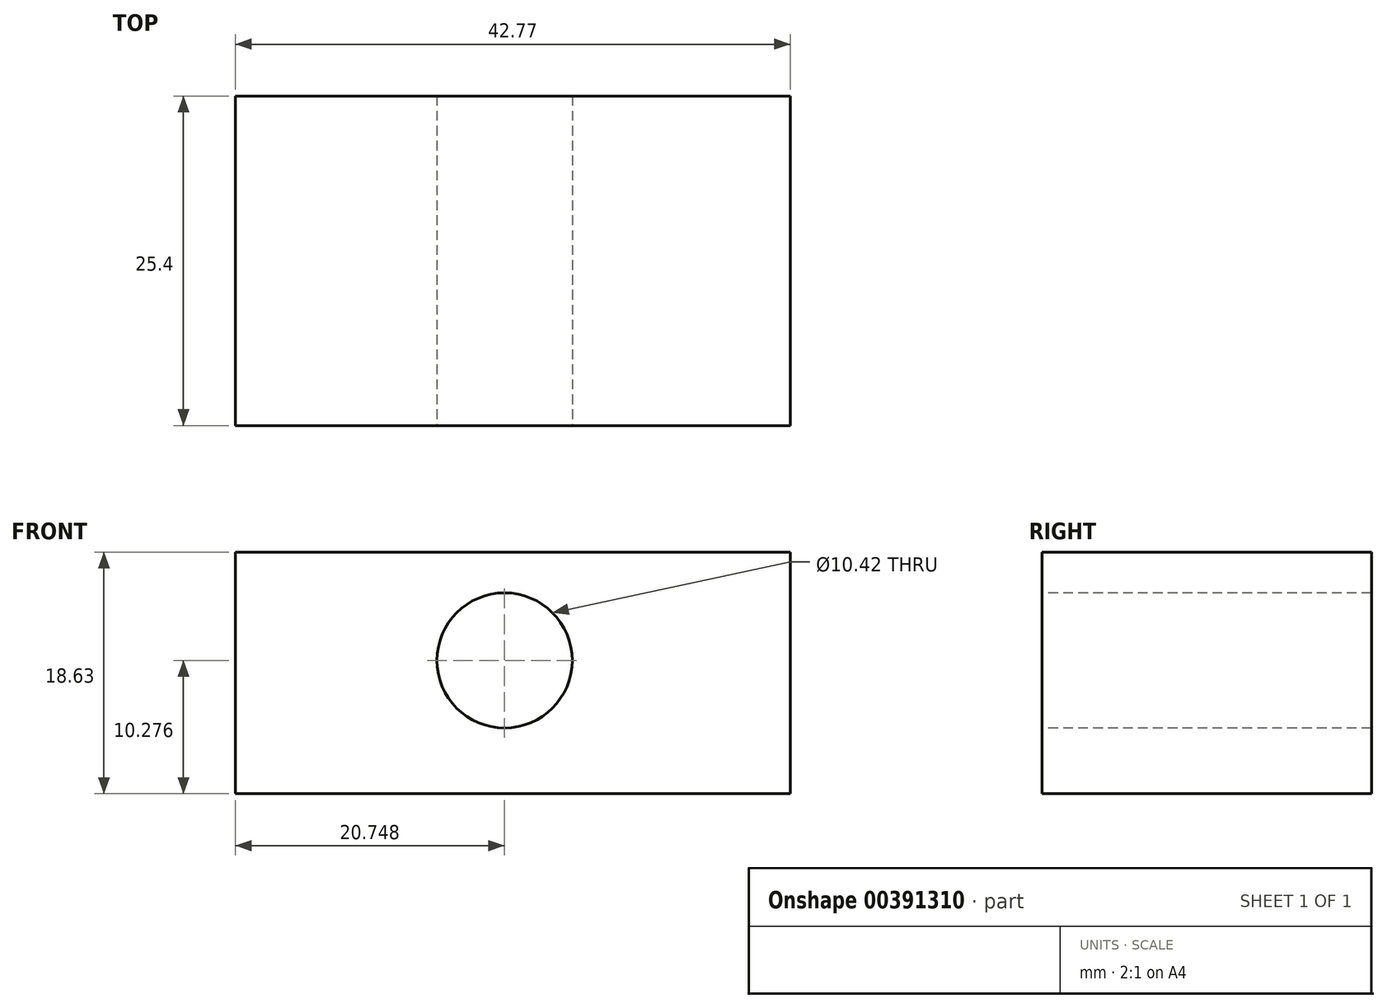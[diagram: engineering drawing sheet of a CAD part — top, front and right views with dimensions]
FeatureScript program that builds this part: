
annotation { "Feature Type Name" : "Feature", "Feature Type Description" : "" }
export const myFeature = defineFeature(function(context is Context, id is Id, definition is map)
    precondition{}
    {
        {
            var Q0;
            Q0=qCreatedBy(makeId("Front.planeOp"),FACE);
            var sketch = newSketch(context, id + "F0", { "sketchPlane" : qUnion([Q0])});
            skLineSegment(sketch, "E0.bottom", {"start": v(0, 0) * mm, "end": v(-42.77, 0) * mm});
            skLineSegment(sketch, "E0.top", {"start": v(0, 18.63) * mm, "end": v(-42.77, 18.63) * mm});
            skLineSegment(sketch, "E0.left", {"start": v(0, 0) * mm, "end": v(0, 18.63) * mm});
            skLineSegment(sketch, "E0.right", {"start": v(-42.77, 0) * mm, "end": v(-42.77, 18.63) * mm});
            skCircle(sketch, "E1", {"center": v(-22.02, 10.28) * mm, "radius": 5.2 * mm});
            skSolve(sketch);
        }
        {
            var Q0;
            Q0 = qSketchRegion(id + "F0", true);
            extrude(context, id + "F1", {"entities" : qUnion([Q0]), "oppositeDirection" : true, "depth" : 25.4 * mm});
        }
    });
